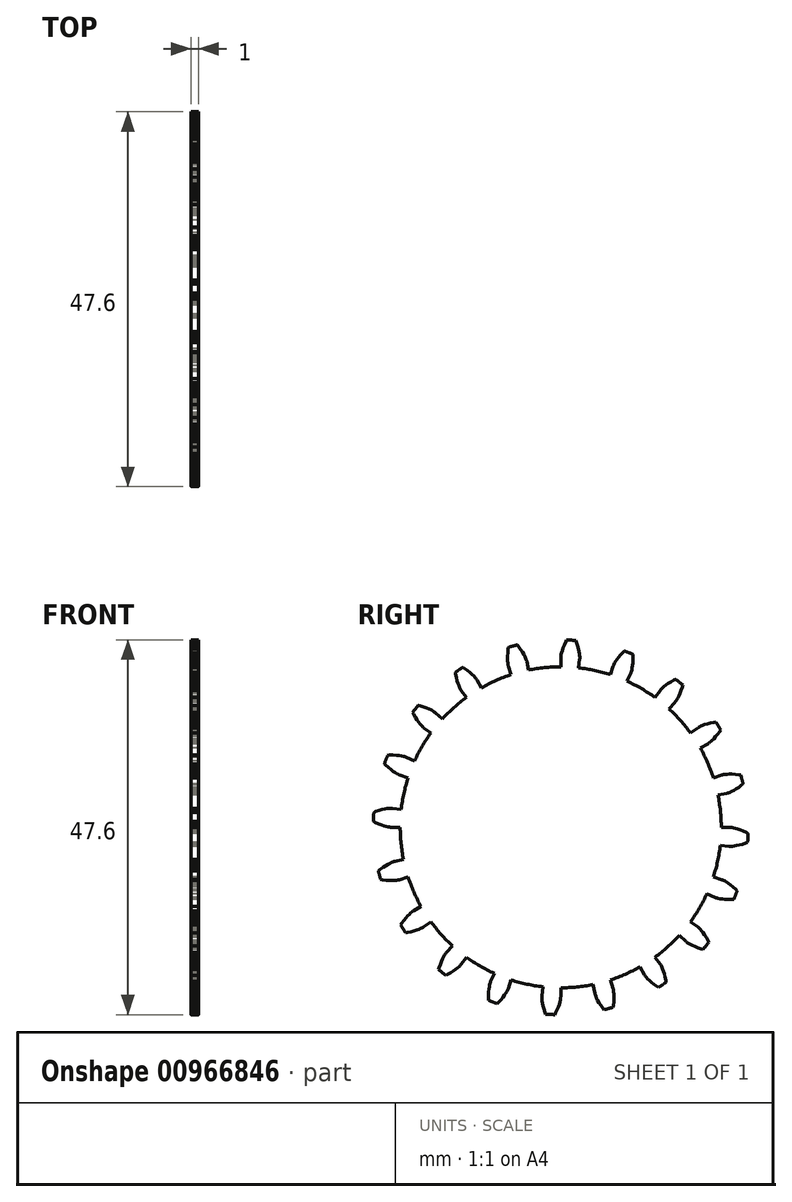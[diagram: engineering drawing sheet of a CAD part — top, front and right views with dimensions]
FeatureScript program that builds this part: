
annotation { "Feature Type Name" : "Feature", "Feature Type Description" : "" }
export const myFeature = defineFeature(function(context is Context, id is Id, definition is map)
    precondition{}
    {
        {
            assignVariable(context, id + "F0", {"name" : "GearThickness", "anyValue" : 1});
        }
        {
            var Q0;
            Q0=qCreatedBy(makeId("Right.planeOp"),FACE);
            var sketch = newSketch(context, id + "F1", { "sketchPlane" : qUnion([Q0])});
            skCircle(sketch, "E0", {"center": v(0, 0) * mm, "radius": 20.39 * mm});
            skCircle(sketch, "E1", {"center": v(0, 0) * mm, "radius": 21.52 * mm, "construction": true});
            skCircle(sketch, "E2", {"center": v(0, 0) * mm, "radius": 22.23 * mm, "construction": true});
            skCircle(sketch, "E3", {"center": v(0, 0) * mm, "radius": 23.81 * mm});
            skLineSegment(sketch, "E4", {"start": v(0, 0) * mm, "end": v(-21.52, 0) * mm, "construction": true});
            skLineSegment(sketch, "E5.1.0", {"start": v(0, 0) * mm, "end": v(-21.5, 1.08) * mm, "construction": true});
            skLineSegment(sketch, "E5.2.0", {"start": v(0, 0) * mm, "end": v(-21.4, 2.15) * mm, "construction": true});
            skLineSegment(sketch, "E5.3.0", {"start": v(0, 0) * mm, "end": v(-21.28, 3.22) * mm, "construction": true});
            skLineSegment(sketch, "E5.4.0", {"start": v(0, 0) * mm, "end": v(-21.09, 4.27) * mm, "construction": true});
            skLineSegment(sketch, "E5.5.0", {"start": v(0, 0) * mm, "end": v(-20.85, 5.32) * mm, "construction": true});
            skLineSegment(sketch, "E5.6.0", {"start": v(0, 0) * mm, "end": v(-20.56, 6.36) * mm, "construction": true});
            skLineSegment(sketch, "E5.7.0", {"start": v(0, 0) * mm, "end": v(-20.21, 7.38) * mm, "construction": true});
            skLineSegment(sketch, "E5.8.0", {"start": v(0, 0) * mm, "end": v(-19.82, 8.38) * mm, "construction": true});
            skLineSegment(sketch, "E5.9.0", {"start": v(0, 0) * mm, "end": v(-19.37, 9.36) * mm, "construction": true});
            skLineSegment(sketch, "E5.10.0", {"start": v(0, 0) * mm, "end": v(-18.88, 10.32) * mm, "construction": true});
            skLineSegment(sketch, "E5.11.0", {"start": v(0, 0) * mm, "end": v(-18.34, 11.25) * mm, "construction": true});
            skLineSegment(sketch, "E5.12.0", {"start": v(0, 0) * mm, "end": v(-17.76, 12.15) * mm, "construction": true});
            skLineSegment(sketch, "E5.13.0", {"start": v(0, 0) * mm, "end": v(-17.13, 13.02) * mm, "construction": true});
            skLineSegment(sketch, "E5.14.0", {"start": v(0, 0) * mm, "end": v(-16.46, 13.86) * mm, "construction": true});
            skLineSegment(sketch, "E5.anchor2", {"start": v(0, 0) * mm, "end": v(-16.46, 13.86) * mm, "construction": true});
            skLineSegment(sketch, "E6", {"start": v(-21.5, 1.08) * mm, "end": v(-21.54, 0) * mm, "construction": true});
            skLineSegment(sketch, "E7", {"start": v(-21.4, 2.15) * mm, "end": v(-21.62, 0) * mm, "construction": true});
            skLineSegment(sketch, "E8", {"start": v(-21.28, 3.22) * mm, "end": v(-21.76, 0.02) * mm, "construction": true});
            skLineSegment(sketch, "E9", {"start": v(-20.85, 5.32) * mm, "end": v(-22.18, 0.11) * mm, "construction": true});
            skLineSegment(sketch, "E10", {"start": v(-20.56, 6.36) * mm, "end": v(-22.46, 0.2) * mm, "construction": true});
            skLineSegment(sketch, "E11", {"start": v(-20.21, 7.38) * mm, "end": v(-22.8, 0.3) * mm, "construction": true});
            skLineSegment(sketch, "E12", {"start": v(-19.82, 8.38) * mm, "end": v(-23.17, 0.45) * mm, "construction": true});
            skLineSegment(sketch, "E13", {"start": v(-19.37, 9.36) * mm, "end": v(-23.59, 0.64) * mm, "construction": true});
            skLineSegment(sketch, "E14", {"start": v(-18.88, 10.32) * mm, "end": v(-24.04, 0.87) * mm, "construction": true});
            skLineSegment(sketch, "E15", {"start": v(-18.34, 11.25) * mm, "end": v(-24.53, 1.16) * mm, "construction": true});
            skLineSegment(sketch, "E16", {"start": v(-21.09, 4.27) * mm, "end": v(-21.94, 0.06) * mm, "construction": true});
            skLineSegment(sketch, "E17", {"start": v(-17.76, 12.15) * mm, "end": v(-25.05, 1.5) * mm, "construction": true});
            skLineSegment(sketch, "E18", {"start": v(-17.13, 13.02) * mm, "end": v(-25.6, 1.89) * mm, "construction": true});
            skLineSegment(sketch, "E19", {"start": v(-16.46, 13.86) * mm, "end": v(-26.16, 2.34) * mm, "construction": true});
            skLineSegment(sketch, "E20", {"start": v(0, 0) * mm, "end": v(-21.48, 1.2) * mm, "construction": true});
            skLineSegment(sketch, "E21", {"start": v(-20.39, 0) * mm, "end": v(-21.52, 0) * mm});
            skLineSegment(sketch, "E22.MirrorCS", {"start": v(-20.26, 2.28) * mm, "end": v(-21.38, 2.4) * mm});
            skLineSegment(sketch, "E23", {"start": v(-21.52, 0) * mm, "end": v(-21.54, 0) * mm});
            skLineSegment(sketch, "E24", {"start": v(-21.54, 0) * mm, "end": v(-21.62, 0) * mm});
            skLineSegment(sketch, "E25", {"start": v(-21.62, 0) * mm, "end": v(-21.76, 0.02) * mm});
            skLineSegment(sketch, "E26", {"start": v(-21.76, 0.02) * mm, "end": v(-21.94, 0.06) * mm});
            skLineSegment(sketch, "E27", {"start": v(-21.94, 0.06) * mm, "end": v(-22.18, 0.11) * mm});
            skLineSegment(sketch, "E28", {"start": v(-22.18, 0.11) * mm, "end": v(-22.46, 0.2) * mm});
            skLineSegment(sketch, "E29", {"start": v(-22.46, 0.2) * mm, "end": v(-22.8, 0.3) * mm});
            skLineSegment(sketch, "E30", {"start": v(-22.8, 0.3) * mm, "end": v(-23.17, 0.45) * mm});
            skLineSegment(sketch, "E31", {"start": v(-23.17, 0.45) * mm, "end": v(-23.59, 0.64) * mm});
            skLineSegment(sketch, "E32", {"start": v(-23.59, 0.64) * mm, "end": v(-24.04, 0.87) * mm});
            skLineSegment(sketch, "E33", {"start": v(-24.04, 0.87) * mm, "end": v(-24.53, 1.16) * mm});
            skLineSegment(sketch, "E34", {"start": v(-24.53, 1.16) * mm, "end": v(-25.05, 1.5) * mm});
            skLineSegment(sketch, "E35", {"start": v(-25.05, 1.5) * mm, "end": v(-25.6, 1.89) * mm});
            skLineSegment(sketch, "E36", {"start": v(-25.6, 1.89) * mm, "end": v(-26.16, 2.34) * mm});
            skLineSegment(sketch, "E37.MirrorCS", {"start": v(-21.38, 2.4) * mm, "end": v(-21.4, 2.41) * mm});
            skLineSegment(sketch, "E38.MirrorCS", {"start": v(-21.4, 2.41) * mm, "end": v(-21.49, 2.41) * mm});
            skLineSegment(sketch, "E39.MirrorCS", {"start": v(-21.49, 2.41) * mm, "end": v(-21.62, 2.41) * mm});
            skLineSegment(sketch, "E40.MirrorCS", {"start": v(-21.62, 2.41) * mm, "end": v(-21.81, 2.4) * mm});
            skLineSegment(sketch, "E41.MirrorCS", {"start": v(-22.05, 2.37) * mm, "end": v(-22.34, 2.32) * mm});
            skLineSegment(sketch, "E42.MirrorCS", {"start": v(-22.34, 2.32) * mm, "end": v(-22.69, 2.25) * mm});
            skLineSegment(sketch, "E43.MirrorCS", {"start": v(-22.69, 2.25) * mm, "end": v(-23.08, 2.15) * mm});
            skLineSegment(sketch, "E44.MirrorCS", {"start": v(-23.08, 2.15) * mm, "end": v(-23.51, 2) * mm});
            skLineSegment(sketch, "E45.MirrorCS", {"start": v(-23.99, 1.82) * mm, "end": v(-24.5, 1.6) * mm});
            skLineSegment(sketch, "E46.MirrorCS", {"start": v(-23.51, 2) * mm, "end": v(-23.99, 1.82) * mm});
            skLineSegment(sketch, "E47.MirrorCS", {"start": v(-24.5, 1.6) * mm, "end": v(-25.06, 1.32) * mm});
            skLineSegment(sketch, "E48.MirrorCS", {"start": v(-25.06, 1.32) * mm, "end": v(-25.64, 0.99) * mm});
            skLineSegment(sketch, "E49.MirrorCS", {"start": v(-25.64, 0.99) * mm, "end": v(-26.26, 0.6) * mm});
            skLineSegment(sketch, "E50.MirrorCS", {"start": v(-21.81, 2.4) * mm, "end": v(-22.05, 2.37) * mm});
            skLineSegment(sketch, "E51.1.0", {"start": v(-19.4, -6.3) * mm, "end": v(-20.46, -6.65) * mm});
            skLineSegment(sketch, "E51.1.1", {"start": v(-23.8, -6.05) * mm, "end": v(-24.24, -6.49) * mm});
            skLineSegment(sketch, "E51.1.2", {"start": v(-19.97, -4.09) * mm, "end": v(-21.08, -4.32) * mm});
            skLineSegment(sketch, "E51.1.3", {"start": v(-23.38, -5.68) * mm, "end": v(-23.8, -6.05) * mm});
            skLineSegment(sketch, "E51.1.4", {"start": v(-23.13, -6.6) * mm, "end": v(-23.69, -6.48) * mm});
            skLineSegment(sketch, "E51.1.5", {"start": v(-23.69, -6.48) * mm, "end": v(-24.28, -6.32) * mm});
            skLineSegment(sketch, "E51.1.6", {"start": v(-22.98, -5.36) * mm, "end": v(-23.38, -5.68) * mm});
            skLineSegment(sketch, "E51.1.7", {"start": v(-24.7, -6.98) * mm, "end": v(-25.16, -7.54) * mm});
            skLineSegment(sketch, "E51.1.8", {"start": v(-22.6, -5.1) * mm, "end": v(-22.98, -5.36) * mm});
            skLineSegment(sketch, "E51.1.9", {"start": v(-24.92, -6.11) * mm, "end": v(-25.6, -5.86) * mm});
            skLineSegment(sketch, "E51.1.10", {"start": v(-24.24, -6.49) * mm, "end": v(-24.7, -6.98) * mm});
            skLineSegment(sketch, "E51.1.11", {"start": v(-22.63, -6.68) * mm, "end": v(-23.13, -6.6) * mm});
            skLineSegment(sketch, "E51.1.12", {"start": v(-24.28, -6.32) * mm, "end": v(-24.92, -6.11) * mm});
            skLineSegment(sketch, "E51.1.13", {"start": v(-21.7, -4.56) * mm, "end": v(-21.97, -4.7) * mm});
            skLineSegment(sketch, "E51.1.14", {"start": v(-21.97, -4.7) * mm, "end": v(-22.27, -4.87) * mm});
            skLineSegment(sketch, "E51.1.15", {"start": v(-22.27, -4.87) * mm, "end": v(-22.6, -5.1) * mm});
            skLineSegment(sketch, "E51.1.16", {"start": v(-21.77, -6.76) * mm, "end": v(-22.18, -6.73) * mm});
            skLineSegment(sketch, "E51.1.17", {"start": v(-21.42, -6.76) * mm, "end": v(-21.77, -6.76) * mm});
            skLineSegment(sketch, "E51.1.18", {"start": v(-22.18, -6.73) * mm, "end": v(-22.63, -6.68) * mm});
            skLineSegment(sketch, "E51.1.19", {"start": v(-21.49, -4.46) * mm, "end": v(-21.7, -4.56) * mm});
            skLineSegment(sketch, "E51.1.20", {"start": v(-21.31, -4.39) * mm, "end": v(-21.49, -4.46) * mm});
            skLineSegment(sketch, "E51.1.21", {"start": v(-21.13, -6.75) * mm, "end": v(-21.42, -6.76) * mm});
            skLineSegment(sketch, "E51.1.22", {"start": v(-20.89, -6.73) * mm, "end": v(-21.13, -6.75) * mm});
            skLineSegment(sketch, "E51.1.23", {"start": v(-20.57, -6.68) * mm, "end": v(-20.7, -6.7) * mm});
            skLineSegment(sketch, "E51.1.24", {"start": v(-21.08, -4.32) * mm, "end": v(-21.1, -4.32) * mm});
            skLineSegment(sketch, "E51.1.25", {"start": v(-21.1, -4.32) * mm, "end": v(-21.18, -4.34) * mm});
            skLineSegment(sketch, "E51.1.26", {"start": v(-20.7, -6.7) * mm, "end": v(-20.89, -6.73) * mm});
            skLineSegment(sketch, "E51.1.27", {"start": v(-21.18, -4.34) * mm, "end": v(-21.31, -4.39) * mm});
            skLineSegment(sketch, "E51.1.28", {"start": v(-20.49, -6.66) * mm, "end": v(-20.57, -6.68) * mm});
            skLineSegment(sketch, "E51.1.29", {"start": v(-20.46, -6.65) * mm, "end": v(-20.49, -6.66) * mm});
            skLineSegment(sketch, "E51.2.0", {"start": v(-16.5, -11.98) * mm, "end": v(-17.4, -12.65) * mm});
            skLineSegment(sketch, "E51.2.1", {"start": v(-20.76, -13.11) * mm, "end": v(-21.05, -13.66) * mm});
            skLineSegment(sketch, "E51.2.2", {"start": v(-17.73, -10.06) * mm, "end": v(-18.71, -10.62) * mm});
            skLineSegment(sketch, "E51.2.3", {"start": v(-20.48, -12.62) * mm, "end": v(-20.76, -13.11) * mm});
            skLineSegment(sketch, "E51.2.4", {"start": v(-19.96, -13.42) * mm, "end": v(-20.53, -13.48) * mm});
            skLineSegment(sketch, "E51.2.5", {"start": v(-20.53, -13.48) * mm, "end": v(-21.14, -13.51) * mm});
            skLineSegment(sketch, "E51.2.6", {"start": v(-20.2, -12.2) * mm, "end": v(-20.48, -12.62) * mm});
            skLineSegment(sketch, "E51.2.7", {"start": v(-21.33, -14.27) * mm, "end": v(-21.6, -14.95) * mm});
            skLineSegment(sketch, "E51.2.8", {"start": v(-19.93, -11.83) * mm, "end": v(-20.2, -12.2) * mm});
            skLineSegment(sketch, "E51.2.9", {"start": v(-21.82, -13.52) * mm, "end": v(-22.54, -13.48) * mm});
            skLineSegment(sketch, "E51.2.10", {"start": v(-21.05, -13.66) * mm, "end": v(-21.33, -14.27) * mm});
            skLineSegment(sketch, "E51.2.11", {"start": v(-19.46, -13.35) * mm, "end": v(-19.96, -13.42) * mm});
            skLineSegment(sketch, "E51.2.12", {"start": v(-21.14, -13.51) * mm, "end": v(-21.82, -13.52) * mm});
            skLineSegment(sketch, "E51.2.13", {"start": v(-19.24, -11.04) * mm, "end": v(-19.44, -11.25) * mm});
            skLineSegment(sketch, "E51.2.14", {"start": v(-19.44, -11.25) * mm, "end": v(-19.68, -11.51) * mm});
            skLineSegment(sketch, "E51.2.15", {"start": v(-19.68, -11.51) * mm, "end": v(-19.93, -11.83) * mm});
            skLineSegment(sketch, "E51.2.16", {"start": v(-18.62, -13.15) * mm, "end": v(-19.01, -13.25) * mm});
            skLineSegment(sketch, "E51.2.17", {"start": v(-18.29, -13.05) * mm, "end": v(-18.62, -13.15) * mm});
            skLineSegment(sketch, "E51.2.18", {"start": v(-19.01, -13.25) * mm, "end": v(-19.46, -13.35) * mm});
            skLineSegment(sketch, "E51.2.19", {"start": v(-19.06, -10.88) * mm, "end": v(-19.24, -11.04) * mm});
            skLineSegment(sketch, "E51.2.20", {"start": v(-18.91, -10.76) * mm, "end": v(-19.06, -10.88) * mm});
            skLineSegment(sketch, "E51.2.21", {"start": v(-18, -12.95) * mm, "end": v(-18.29, -13.05) * mm});
            skLineSegment(sketch, "E51.2.22", {"start": v(-17.79, -12.85) * mm, "end": v(-18, -12.95) * mm});
            skLineSegment(sketch, "E51.2.23", {"start": v(-17.5, -12.7) * mm, "end": v(-17.62, -12.77) * mm});
            skLineSegment(sketch, "E51.2.24", {"start": v(-18.71, -10.62) * mm, "end": v(-18.74, -10.63) * mm});
            skLineSegment(sketch, "E51.2.25", {"start": v(-18.74, -10.63) * mm, "end": v(-18.8, -10.68) * mm});
            skLineSegment(sketch, "E51.2.26", {"start": v(-17.62, -12.77) * mm, "end": v(-17.79, -12.85) * mm});
            skLineSegment(sketch, "E51.2.27", {"start": v(-18.8, -10.68) * mm, "end": v(-18.91, -10.76) * mm});
            skLineSegment(sketch, "E51.2.28", {"start": v(-17.43, -12.66) * mm, "end": v(-17.5, -12.7) * mm});
            skLineSegment(sketch, "E51.2.29", {"start": v(-17.4, -12.65) * mm, "end": v(-17.43, -12.66) * mm});
            skLineSegment(sketch, "E51.3.0", {"start": v(-11.98, -16.5) * mm, "end": v(-12.65, -17.4) * mm});
            skLineSegment(sketch, "E51.3.1", {"start": v(-15.7, -18.89) * mm, "end": v(-15.8, -19.5) * mm});
            skLineSegment(sketch, "E51.3.2", {"start": v(-13.76, -15.05) * mm, "end": v(-14.52, -15.88) * mm});
            skLineSegment(sketch, "E51.3.3", {"start": v(-15.57, -18.33) * mm, "end": v(-15.7, -18.89) * mm});
            skLineSegment(sketch, "E51.3.4", {"start": v(-14.84, -18.94) * mm, "end": v(-15.35, -19.16) * mm});
            skLineSegment(sketch, "E51.3.5", {"start": v(-15.35, -19.16) * mm, "end": v(-15.93, -19.39) * mm});
            skLineSegment(sketch, "E51.3.6", {"start": v(-15.44, -17.84) * mm, "end": v(-15.57, -18.33) * mm});
            skLineSegment(sketch, "E51.3.7", {"start": v(-15.87, -20.16) * mm, "end": v(-15.92, -20.89) * mm});
            skLineSegment(sketch, "E51.3.8", {"start": v(-15.3, -17.4) * mm, "end": v(-15.44, -17.84) * mm});
            skLineSegment(sketch, "E51.3.9", {"start": v(-16.57, -19.6) * mm, "end": v(-17.27, -19.79) * mm});
            skLineSegment(sketch, "E51.3.10", {"start": v(-15.8, -19.5) * mm, "end": v(-15.87, -20.16) * mm});
            skLineSegment(sketch, "E51.3.11", {"start": v(-14.38, -18.7) * mm, "end": v(-14.84, -18.94) * mm});
            skLineSegment(sketch, "E51.3.12", {"start": v(-15.93, -19.39) * mm, "end": v(-16.57, -19.6) * mm});
            skLineSegment(sketch, "E51.3.13", {"start": v(-14.88, -16.45) * mm, "end": v(-15.01, -16.71) * mm});
            skLineSegment(sketch, "E51.3.14", {"start": v(-15.01, -16.71) * mm, "end": v(-15.15, -17.03) * mm});
            skLineSegment(sketch, "E51.3.15", {"start": v(-15.15, -17.03) * mm, "end": v(-15.3, -17.4) * mm});
            skLineSegment(sketch, "E51.3.16", {"start": v(-13.64, -18.26) * mm, "end": v(-13.98, -18.48) * mm});
            skLineSegment(sketch, "E51.3.17", {"start": v(-13.36, -18.06) * mm, "end": v(-13.64, -18.26) * mm});
            skLineSegment(sketch, "E51.3.18", {"start": v(-13.98, -18.48) * mm, "end": v(-14.38, -18.7) * mm});
            skLineSegment(sketch, "E51.3.19", {"start": v(-14.76, -16.24) * mm, "end": v(-14.88, -16.45) * mm});
            skLineSegment(sketch, "E51.3.20", {"start": v(-14.66, -16.08) * mm, "end": v(-14.76, -16.24) * mm});
            skLineSegment(sketch, "E51.3.21", {"start": v(-13.13, -17.88) * mm, "end": v(-13.36, -18.06) * mm});
            skLineSegment(sketch, "E51.3.22", {"start": v(-12.94, -17.72) * mm, "end": v(-13.13, -17.88) * mm});
            skLineSegment(sketch, "E51.3.23", {"start": v(-12.72, -17.5) * mm, "end": v(-12.8, -17.59) * mm});
            skLineSegment(sketch, "E51.3.24", {"start": v(-14.52, -15.88) * mm, "end": v(-14.53, -15.9) * mm});
            skLineSegment(sketch, "E51.3.25", {"start": v(-14.53, -15.9) * mm, "end": v(-14.58, -15.97) * mm});
            skLineSegment(sketch, "E51.3.26", {"start": v(-12.8, -17.59) * mm, "end": v(-12.94, -17.72) * mm});
            skLineSegment(sketch, "E51.3.27", {"start": v(-14.58, -15.97) * mm, "end": v(-14.66, -16.08) * mm});
            skLineSegment(sketch, "E51.3.28", {"start": v(-12.66, -17.43) * mm, "end": v(-12.72, -17.5) * mm});
            skLineSegment(sketch, "E51.3.29", {"start": v(-12.65, -17.4) * mm, "end": v(-12.66, -17.43) * mm});
            skLineSegment(sketch, "E51.4.0", {"start": v(-6.3, -19.4) * mm, "end": v(-6.65, -20.46) * mm});
            skLineSegment(sketch, "E51.4.1", {"start": v(-9.1, -22.81) * mm, "end": v(-9, -23.42) * mm});
            skLineSegment(sketch, "E51.4.2", {"start": v(-8.43, -18.56) * mm, "end": v(-8.9, -19.6) * mm});
            skLineSegment(sketch, "E51.4.3", {"start": v(-9.15, -22.25) * mm, "end": v(-9.1, -22.81) * mm});
            skLineSegment(sketch, "E51.4.4", {"start": v(-8.26, -22.6) * mm, "end": v(-8.68, -22.97) * mm});
            skLineSegment(sketch, "E51.4.5", {"start": v(-8.68, -22.97) * mm, "end": v(-9.16, -23.36) * mm});
            skLineSegment(sketch, "E51.4.6", {"start": v(-9.17, -21.74) * mm, "end": v(-9.15, -22.25) * mm});
            skLineSegment(sketch, "E51.4.7", {"start": v(-8.87, -24.08) * mm, "end": v(-8.69, -24.79) * mm});
            skLineSegment(sketch, "E51.4.8", {"start": v(-9.17, -21.28) * mm, "end": v(-9.17, -21.74) * mm});
            skLineSegment(sketch, "E51.4.9", {"start": v(-9.7, -23.76) * mm, "end": v(-10.31, -24.16) * mm});
            skLineSegment(sketch, "E51.4.10", {"start": v(-9, -23.42) * mm, "end": v(-8.87, -24.08) * mm});
            skLineSegment(sketch, "E51.4.11", {"start": v(-7.9, -22.23) * mm, "end": v(-8.26, -22.6) * mm});
            skLineSegment(sketch, "E51.4.12", {"start": v(-9.16, -23.36) * mm, "end": v(-9.7, -23.76) * mm});
            skLineSegment(sketch, "E51.4.13", {"start": v(-9.07, -20.24) * mm, "end": v(-9.12, -20.53) * mm});
            skLineSegment(sketch, "E51.4.14", {"start": v(-9.12, -20.53) * mm, "end": v(-9.15, -20.88) * mm});
            skLineSegment(sketch, "E51.4.15", {"start": v(-9.15, -20.88) * mm, "end": v(-9.17, -21.28) * mm});
            skLineSegment(sketch, "E51.4.16", {"start": v(-7.33, -21.59) * mm, "end": v(-7.59, -21.9) * mm});
            skLineSegment(sketch, "E51.4.17", {"start": v(-7.12, -21.3) * mm, "end": v(-7.33, -21.59) * mm});
            skLineSegment(sketch, "E51.4.18", {"start": v(-7.59, -21.9) * mm, "end": v(-7.9, -22.23) * mm});
            skLineSegment(sketch, "E51.4.19", {"start": v(-9.02, -20) * mm, "end": v(-9.07, -20.24) * mm});
            skLineSegment(sketch, "E51.4.20", {"start": v(-8.98, -19.82) * mm, "end": v(-9.02, -20) * mm});
            skLineSegment(sketch, "E51.4.21", {"start": v(-6.96, -21.06) * mm, "end": v(-7.12, -21.3) * mm});
            skLineSegment(sketch, "E51.4.22", {"start": v(-6.84, -20.85) * mm, "end": v(-6.96, -21.06) * mm});
            skLineSegment(sketch, "E51.4.23", {"start": v(-6.69, -20.56) * mm, "end": v(-6.75, -20.69) * mm});
            skLineSegment(sketch, "E51.4.24", {"start": v(-8.9, -19.6) * mm, "end": v(-8.9, -19.62) * mm});
            skLineSegment(sketch, "E51.4.25", {"start": v(-8.9, -19.62) * mm, "end": v(-8.94, -19.7) * mm});
            skLineSegment(sketch, "E51.4.26", {"start": v(-6.75, -20.69) * mm, "end": v(-6.84, -20.85) * mm});
            skLineSegment(sketch, "E51.4.27", {"start": v(-8.94, -19.7) * mm, "end": v(-8.98, -19.82) * mm});
            skLineSegment(sketch, "E51.4.28", {"start": v(-6.66, -20.49) * mm, "end": v(-6.69, -20.56) * mm});
            skLineSegment(sketch, "E51.4.29", {"start": v(-6.65, -20.46) * mm, "end": v(-6.66, -20.49) * mm});
            skLineSegment(sketch, "E51.5.0", {"start": v(0, -20.39) * mm, "end": v(0, -21.52) * mm});
            skLineSegment(sketch, "E51.5.1", {"start": v(-1.6, -24.5) * mm, "end": v(-1.32, -25.06) * mm});
            skLineSegment(sketch, "E51.5.2", {"start": v(-2.28, -20.26) * mm, "end": v(-2.4, -21.38) * mm});
            skLineSegment(sketch, "E51.5.3", {"start": v(-1.82, -23.99) * mm, "end": v(-1.6, -24.5) * mm});
            skLineSegment(sketch, "E51.5.4", {"start": v(-0.87, -24.04) * mm, "end": v(-1.16, -24.53) * mm});
            skLineSegment(sketch, "E51.5.5", {"start": v(-1.16, -24.53) * mm, "end": v(-1.5, -25.05) * mm});
            skLineSegment(sketch, "E51.5.6", {"start": v(-2, -23.51) * mm, "end": v(-1.82, -23.99) * mm});
            skLineSegment(sketch, "E51.5.7", {"start": v(-0.99, -25.64) * mm, "end": v(-0.6, -26.26) * mm});
            skLineSegment(sketch, "E51.5.8", {"start": v(-2.15, -23.08) * mm, "end": v(-2, -23.51) * mm});
            skLineSegment(sketch, "E51.5.9", {"start": v(-1.89, -25.6) * mm, "end": v(-2.34, -26.16) * mm});
            skLineSegment(sketch, "E51.5.10", {"start": v(-1.32, -25.06) * mm, "end": v(-0.99, -25.64) * mm});
            skLineSegment(sketch, "E51.5.11", {"start": v(-0.64, -23.59) * mm, "end": v(-0.87, -24.04) * mm});
            skLineSegment(sketch, "E51.5.12", {"start": v(-1.5, -25.05) * mm, "end": v(-1.89, -25.6) * mm});
            skLineSegment(sketch, "E51.5.13", {"start": v(-2.37, -22.05) * mm, "end": v(-2.32, -22.34) * mm});
            skLineSegment(sketch, "E51.5.14", {"start": v(-2.32, -22.34) * mm, "end": v(-2.25, -22.69) * mm});
            skLineSegment(sketch, "E51.5.15", {"start": v(-2.25, -22.69) * mm, "end": v(-2.15, -23.08) * mm});
            skLineSegment(sketch, "E51.5.16", {"start": v(-0.3, -22.8) * mm, "end": v(-0.45, -23.17) * mm});
            skLineSegment(sketch, "E51.5.17", {"start": v(-0.2, -22.46) * mm, "end": v(-0.3, -22.8) * mm});
            skLineSegment(sketch, "E51.5.18", {"start": v(-0.45, -23.17) * mm, "end": v(-0.64, -23.59) * mm});
            skLineSegment(sketch, "E51.5.19", {"start": v(-2.4, -21.81) * mm, "end": v(-2.37, -22.05) * mm});
            skLineSegment(sketch, "E51.5.20", {"start": v(-2.41, -21.62) * mm, "end": v(-2.4, -21.81) * mm});
            skLineSegment(sketch, "E51.5.21", {"start": v(-0.11, -22.18) * mm, "end": v(-0.2, -22.46) * mm});
            skLineSegment(sketch, "E51.5.22", {"start": v(-0.06, -21.94) * mm, "end": v(-0.11, -22.18) * mm});
            skLineSegment(sketch, "E51.5.23", {"start": v(0, -21.62) * mm, "end": v(-0.02, -21.76) * mm});
            skLineSegment(sketch, "E51.5.24", {"start": v(-2.4, -21.38) * mm, "end": v(-2.41, -21.4) * mm});
            skLineSegment(sketch, "E51.5.25", {"start": v(-2.41, -21.4) * mm, "end": v(-2.41, -21.49) * mm});
            skLineSegment(sketch, "E51.5.26", {"start": v(-0.02, -21.76) * mm, "end": v(-0.06, -21.94) * mm});
            skLineSegment(sketch, "E51.5.27", {"start": v(-2.41, -21.49) * mm, "end": v(-2.41, -21.62) * mm});
            skLineSegment(sketch, "E51.5.28", {"start": v(0, -21.54) * mm, "end": v(0, -21.62) * mm});
            skLineSegment(sketch, "E51.5.29", {"start": v(0, -21.52) * mm, "end": v(0, -21.54) * mm});
            skLineSegment(sketch, "E51.6.0", {"start": v(6.3, -19.4) * mm, "end": v(6.65, -20.46) * mm});
            skLineSegment(sketch, "E51.6.1", {"start": v(6.05, -23.8) * mm, "end": v(6.49, -24.24) * mm});
            skLineSegment(sketch, "E51.6.2", {"start": v(4.09, -19.97) * mm, "end": v(4.32, -21.08) * mm});
            skLineSegment(sketch, "E51.6.3", {"start": v(5.68, -23.38) * mm, "end": v(6.05, -23.8) * mm});
            skLineSegment(sketch, "E51.6.4", {"start": v(6.6, -23.13) * mm, "end": v(6.48, -23.69) * mm});
            skLineSegment(sketch, "E51.6.5", {"start": v(6.48, -23.69) * mm, "end": v(6.32, -24.28) * mm});
            skLineSegment(sketch, "E51.6.6", {"start": v(5.36, -22.98) * mm, "end": v(5.68, -23.38) * mm});
            skLineSegment(sketch, "E51.6.7", {"start": v(6.98, -24.7) * mm, "end": v(7.54, -25.16) * mm});
            skLineSegment(sketch, "E51.6.8", {"start": v(5.1, -22.6) * mm, "end": v(5.36, -22.98) * mm});
            skLineSegment(sketch, "E51.6.9", {"start": v(6.11, -24.92) * mm, "end": v(5.86, -25.6) * mm});
            skLineSegment(sketch, "E51.6.10", {"start": v(6.49, -24.24) * mm, "end": v(6.98, -24.7) * mm});
            skLineSegment(sketch, "E51.6.11", {"start": v(6.68, -22.63) * mm, "end": v(6.6, -23.13) * mm});
            skLineSegment(sketch, "E51.6.12", {"start": v(6.32, -24.28) * mm, "end": v(6.11, -24.92) * mm});
            skLineSegment(sketch, "E51.6.13", {"start": v(4.56, -21.7) * mm, "end": v(4.7, -21.97) * mm});
            skLineSegment(sketch, "E51.6.14", {"start": v(4.7, -21.97) * mm, "end": v(4.87, -22.27) * mm});
            skLineSegment(sketch, "E51.6.15", {"start": v(4.87, -22.27) * mm, "end": v(5.1, -22.6) * mm});
            skLineSegment(sketch, "E51.6.16", {"start": v(6.76, -21.77) * mm, "end": v(6.73, -22.18) * mm});
            skLineSegment(sketch, "E51.6.17", {"start": v(6.76, -21.42) * mm, "end": v(6.76, -21.77) * mm});
            skLineSegment(sketch, "E51.6.18", {"start": v(6.73, -22.18) * mm, "end": v(6.68, -22.63) * mm});
            skLineSegment(sketch, "E51.6.19", {"start": v(4.46, -21.49) * mm, "end": v(4.56, -21.7) * mm});
            skLineSegment(sketch, "E51.6.20", {"start": v(4.39, -21.31) * mm, "end": v(4.46, -21.49) * mm});
            skLineSegment(sketch, "E51.6.21", {"start": v(6.75, -21.13) * mm, "end": v(6.76, -21.42) * mm});
            skLineSegment(sketch, "E51.6.22", {"start": v(6.73, -20.89) * mm, "end": v(6.75, -21.13) * mm});
            skLineSegment(sketch, "E51.6.23", {"start": v(6.68, -20.57) * mm, "end": v(6.7, -20.7) * mm});
            skLineSegment(sketch, "E51.6.24", {"start": v(4.32, -21.08) * mm, "end": v(4.32, -21.1) * mm});
            skLineSegment(sketch, "E51.6.25", {"start": v(4.32, -21.1) * mm, "end": v(4.34, -21.18) * mm});
            skLineSegment(sketch, "E51.6.26", {"start": v(6.7, -20.7) * mm, "end": v(6.73, -20.89) * mm});
            skLineSegment(sketch, "E51.6.27", {"start": v(4.34, -21.18) * mm, "end": v(4.39, -21.31) * mm});
            skLineSegment(sketch, "E51.6.28", {"start": v(6.66, -20.49) * mm, "end": v(6.68, -20.57) * mm});
            skLineSegment(sketch, "E51.6.29", {"start": v(6.65, -20.46) * mm, "end": v(6.66, -20.49) * mm});
            skLineSegment(sketch, "E51.7.0", {"start": v(11.98, -16.5) * mm, "end": v(12.65, -17.4) * mm});
            skLineSegment(sketch, "E51.7.1", {"start": v(13.11, -20.76) * mm, "end": v(13.66, -21.05) * mm});
            skLineSegment(sketch, "E51.7.2", {"start": v(10.06, -17.73) * mm, "end": v(10.62, -18.71) * mm});
            skLineSegment(sketch, "E51.7.3", {"start": v(12.62, -20.48) * mm, "end": v(13.11, -20.76) * mm});
            skLineSegment(sketch, "E51.7.4", {"start": v(13.42, -19.96) * mm, "end": v(13.48, -20.53) * mm});
            skLineSegment(sketch, "E51.7.5", {"start": v(13.48, -20.53) * mm, "end": v(13.51, -21.14) * mm});
            skLineSegment(sketch, "E51.7.6", {"start": v(12.2, -20.2) * mm, "end": v(12.62, -20.48) * mm});
            skLineSegment(sketch, "E51.7.7", {"start": v(14.27, -21.33) * mm, "end": v(14.95, -21.6) * mm});
            skLineSegment(sketch, "E51.7.8", {"start": v(11.83, -19.93) * mm, "end": v(12.2, -20.2) * mm});
            skLineSegment(sketch, "E51.7.9", {"start": v(13.52, -21.82) * mm, "end": v(13.48, -22.54) * mm});
            skLineSegment(sketch, "E51.7.10", {"start": v(13.66, -21.05) * mm, "end": v(14.27, -21.33) * mm});
            skLineSegment(sketch, "E51.7.11", {"start": v(13.35, -19.46) * mm, "end": v(13.42, -19.96) * mm});
            skLineSegment(sketch, "E51.7.12", {"start": v(13.51, -21.14) * mm, "end": v(13.52, -21.82) * mm});
            skLineSegment(sketch, "E51.7.13", {"start": v(11.04, -19.24) * mm, "end": v(11.25, -19.44) * mm});
            skLineSegment(sketch, "E51.7.14", {"start": v(11.25, -19.44) * mm, "end": v(11.51, -19.68) * mm});
            skLineSegment(sketch, "E51.7.15", {"start": v(11.51, -19.68) * mm, "end": v(11.83, -19.93) * mm});
            skLineSegment(sketch, "E51.7.16", {"start": v(13.15, -18.62) * mm, "end": v(13.25, -19.01) * mm});
            skLineSegment(sketch, "E51.7.17", {"start": v(13.05, -18.29) * mm, "end": v(13.15, -18.62) * mm});
            skLineSegment(sketch, "E51.7.18", {"start": v(13.25, -19.01) * mm, "end": v(13.35, -19.46) * mm});
            skLineSegment(sketch, "E51.7.19", {"start": v(10.88, -19.06) * mm, "end": v(11.04, -19.24) * mm});
            skLineSegment(sketch, "E51.7.20", {"start": v(10.76, -18.91) * mm, "end": v(10.88, -19.06) * mm});
            skLineSegment(sketch, "E51.7.21", {"start": v(12.95, -18) * mm, "end": v(13.05, -18.29) * mm});
            skLineSegment(sketch, "E51.7.22", {"start": v(12.85, -17.79) * mm, "end": v(12.95, -18) * mm});
            skLineSegment(sketch, "E51.7.23", {"start": v(12.7, -17.5) * mm, "end": v(12.77, -17.62) * mm});
            skLineSegment(sketch, "E51.7.24", {"start": v(10.62, -18.71) * mm, "end": v(10.63, -18.74) * mm});
            skLineSegment(sketch, "E51.7.25", {"start": v(10.63, -18.74) * mm, "end": v(10.68, -18.8) * mm});
            skLineSegment(sketch, "E51.7.26", {"start": v(12.77, -17.62) * mm, "end": v(12.85, -17.79) * mm});
            skLineSegment(sketch, "E51.7.27", {"start": v(10.68, -18.8) * mm, "end": v(10.76, -18.91) * mm});
            skLineSegment(sketch, "E51.7.28", {"start": v(12.66, -17.43) * mm, "end": v(12.7, -17.5) * mm});
            skLineSegment(sketch, "E51.7.29", {"start": v(12.65, -17.4) * mm, "end": v(12.66, -17.43) * mm});
            skLineSegment(sketch, "E51.8.0", {"start": v(16.5, -11.98) * mm, "end": v(17.4, -12.65) * mm});
            skLineSegment(sketch, "E51.8.1", {"start": v(18.89, -15.7) * mm, "end": v(19.5, -15.8) * mm});
            skLineSegment(sketch, "E51.8.2", {"start": v(15.05, -13.76) * mm, "end": v(15.88, -14.52) * mm});
            skLineSegment(sketch, "E51.8.3", {"start": v(18.33, -15.57) * mm, "end": v(18.89, -15.7) * mm});
            skLineSegment(sketch, "E51.8.4", {"start": v(18.94, -14.84) * mm, "end": v(19.16, -15.35) * mm});
            skLineSegment(sketch, "E51.8.5", {"start": v(19.16, -15.35) * mm, "end": v(19.39, -15.93) * mm});
            skLineSegment(sketch, "E51.8.6", {"start": v(17.84, -15.44) * mm, "end": v(18.33, -15.57) * mm});
            skLineSegment(sketch, "E51.8.7", {"start": v(20.16, -15.87) * mm, "end": v(20.89, -15.92) * mm});
            skLineSegment(sketch, "E51.8.8", {"start": v(17.4, -15.3) * mm, "end": v(17.84, -15.44) * mm});
            skLineSegment(sketch, "E51.8.9", {"start": v(19.6, -16.57) * mm, "end": v(19.79, -17.27) * mm});
            skLineSegment(sketch, "E51.8.10", {"start": v(19.5, -15.8) * mm, "end": v(20.16, -15.87) * mm});
            skLineSegment(sketch, "E51.8.11", {"start": v(18.7, -14.38) * mm, "end": v(18.94, -14.84) * mm});
            skLineSegment(sketch, "E51.8.12", {"start": v(19.39, -15.93) * mm, "end": v(19.6, -16.57) * mm});
            skLineSegment(sketch, "E51.8.13", {"start": v(16.45, -14.88) * mm, "end": v(16.71, -15.01) * mm});
            skLineSegment(sketch, "E51.8.14", {"start": v(16.71, -15.01) * mm, "end": v(17.03, -15.15) * mm});
            skLineSegment(sketch, "E51.8.15", {"start": v(17.03, -15.15) * mm, "end": v(17.4, -15.3) * mm});
            skLineSegment(sketch, "E51.8.16", {"start": v(18.26, -13.64) * mm, "end": v(18.48, -13.98) * mm});
            skLineSegment(sketch, "E51.8.17", {"start": v(18.06, -13.36) * mm, "end": v(18.26, -13.64) * mm});
            skLineSegment(sketch, "E51.8.18", {"start": v(18.48, -13.98) * mm, "end": v(18.7, -14.38) * mm});
            skLineSegment(sketch, "E51.8.19", {"start": v(16.24, -14.76) * mm, "end": v(16.45, -14.88) * mm});
            skLineSegment(sketch, "E51.8.20", {"start": v(16.08, -14.66) * mm, "end": v(16.24, -14.76) * mm});
            skLineSegment(sketch, "E51.8.21", {"start": v(17.88, -13.13) * mm, "end": v(18.06, -13.36) * mm});
            skLineSegment(sketch, "E51.8.22", {"start": v(17.72, -12.94) * mm, "end": v(17.88, -13.13) * mm});
            skLineSegment(sketch, "E51.8.23", {"start": v(17.5, -12.72) * mm, "end": v(17.59, -12.8) * mm});
            skLineSegment(sketch, "E51.8.24", {"start": v(15.88, -14.52) * mm, "end": v(15.9, -14.53) * mm});
            skLineSegment(sketch, "E51.8.25", {"start": v(15.9, -14.53) * mm, "end": v(15.97, -14.58) * mm});
            skLineSegment(sketch, "E51.8.26", {"start": v(17.59, -12.8) * mm, "end": v(17.72, -12.94) * mm});
            skLineSegment(sketch, "E51.8.27", {"start": v(15.97, -14.58) * mm, "end": v(16.08, -14.66) * mm});
            skLineSegment(sketch, "E51.8.28", {"start": v(17.43, -12.66) * mm, "end": v(17.5, -12.72) * mm});
            skLineSegment(sketch, "E51.8.29", {"start": v(17.4, -12.65) * mm, "end": v(17.43, -12.66) * mm});
            skLineSegment(sketch, "E51.9.0", {"start": v(19.4, -6.3) * mm, "end": v(20.46, -6.65) * mm});
            skLineSegment(sketch, "E51.9.1", {"start": v(22.81, -9.1) * mm, "end": v(23.42, -9) * mm});
            skLineSegment(sketch, "E51.9.2", {"start": v(18.56, -8.43) * mm, "end": v(19.6, -8.9) * mm});
            skLineSegment(sketch, "E51.9.3", {"start": v(22.25, -9.15) * mm, "end": v(22.81, -9.1) * mm});
            skLineSegment(sketch, "E51.9.4", {"start": v(22.6, -8.26) * mm, "end": v(22.97, -8.68) * mm});
            skLineSegment(sketch, "E51.9.5", {"start": v(22.97, -8.68) * mm, "end": v(23.36, -9.16) * mm});
            skLineSegment(sketch, "E51.9.6", {"start": v(21.74, -9.17) * mm, "end": v(22.25, -9.15) * mm});
            skLineSegment(sketch, "E51.9.7", {"start": v(24.08, -8.87) * mm, "end": v(24.79, -8.69) * mm});
            skLineSegment(sketch, "E51.9.8", {"start": v(21.28, -9.17) * mm, "end": v(21.74, -9.17) * mm});
            skLineSegment(sketch, "E51.9.9", {"start": v(23.76, -9.7) * mm, "end": v(24.16, -10.31) * mm});
            skLineSegment(sketch, "E51.9.10", {"start": v(23.42, -9) * mm, "end": v(24.08, -8.87) * mm});
            skLineSegment(sketch, "E51.9.11", {"start": v(22.23, -7.9) * mm, "end": v(22.6, -8.26) * mm});
            skLineSegment(sketch, "E51.9.12", {"start": v(23.36, -9.16) * mm, "end": v(23.76, -9.7) * mm});
            skLineSegment(sketch, "E51.9.13", {"start": v(20.24, -9.07) * mm, "end": v(20.53, -9.12) * mm});
            skLineSegment(sketch, "E51.9.14", {"start": v(20.53, -9.12) * mm, "end": v(20.88, -9.15) * mm});
            skLineSegment(sketch, "E51.9.15", {"start": v(20.88, -9.15) * mm, "end": v(21.28, -9.17) * mm});
            skLineSegment(sketch, "E51.9.16", {"start": v(21.59, -7.33) * mm, "end": v(21.9, -7.59) * mm});
            skLineSegment(sketch, "E51.9.17", {"start": v(21.3, -7.12) * mm, "end": v(21.59, -7.33) * mm});
            skLineSegment(sketch, "E51.9.18", {"start": v(21.9, -7.59) * mm, "end": v(22.23, -7.9) * mm});
            skLineSegment(sketch, "E51.9.19", {"start": v(20, -9.02) * mm, "end": v(20.24, -9.07) * mm});
            skLineSegment(sketch, "E51.9.20", {"start": v(19.82, -8.98) * mm, "end": v(20, -9.02) * mm});
            skLineSegment(sketch, "E51.9.21", {"start": v(21.06, -6.96) * mm, "end": v(21.3, -7.12) * mm});
            skLineSegment(sketch, "E51.9.22", {"start": v(20.85, -6.84) * mm, "end": v(21.06, -6.96) * mm});
            skLineSegment(sketch, "E51.9.23", {"start": v(20.56, -6.69) * mm, "end": v(20.69, -6.75) * mm});
            skLineSegment(sketch, "E51.9.24", {"start": v(19.6, -8.9) * mm, "end": v(19.62, -8.9) * mm});
            skLineSegment(sketch, "E51.9.25", {"start": v(19.62, -8.9) * mm, "end": v(19.7, -8.94) * mm});
            skLineSegment(sketch, "E51.9.26", {"start": v(20.69, -6.75) * mm, "end": v(20.85, -6.84) * mm});
            skLineSegment(sketch, "E51.9.27", {"start": v(19.7, -8.94) * mm, "end": v(19.82, -8.98) * mm});
            skLineSegment(sketch, "E51.9.28", {"start": v(20.49, -6.66) * mm, "end": v(20.56, -6.69) * mm});
            skLineSegment(sketch, "E51.9.29", {"start": v(20.46, -6.65) * mm, "end": v(20.49, -6.66) * mm});
            skLineSegment(sketch, "E51.10.0", {"start": v(20.39, 0) * mm, "end": v(21.52, 0) * mm});
            skLineSegment(sketch, "E51.10.1", {"start": v(24.5, -1.6) * mm, "end": v(25.06, -1.32) * mm});
            skLineSegment(sketch, "E51.10.2", {"start": v(20.26, -2.28) * mm, "end": v(21.38, -2.4) * mm});
            skLineSegment(sketch, "E51.10.3", {"start": v(23.99, -1.82) * mm, "end": v(24.5, -1.6) * mm});
            skLineSegment(sketch, "E51.10.4", {"start": v(24.04, -0.87) * mm, "end": v(24.53, -1.16) * mm});
            skLineSegment(sketch, "E51.10.5", {"start": v(24.53, -1.16) * mm, "end": v(25.05, -1.5) * mm});
            skLineSegment(sketch, "E51.10.6", {"start": v(23.51, -2) * mm, "end": v(23.99, -1.82) * mm});
            skLineSegment(sketch, "E51.10.7", {"start": v(25.64, -0.99) * mm, "end": v(26.26, -0.6) * mm});
            skLineSegment(sketch, "E51.10.8", {"start": v(23.08, -2.15) * mm, "end": v(23.51, -2) * mm});
            skLineSegment(sketch, "E51.10.9", {"start": v(25.6, -1.89) * mm, "end": v(26.16, -2.34) * mm});
            skLineSegment(sketch, "E51.10.10", {"start": v(25.06, -1.32) * mm, "end": v(25.64, -0.99) * mm});
            skLineSegment(sketch, "E51.10.11", {"start": v(23.59, -0.64) * mm, "end": v(24.04, -0.87) * mm});
            skLineSegment(sketch, "E51.10.12", {"start": v(25.05, -1.5) * mm, "end": v(25.6, -1.89) * mm});
            skLineSegment(sketch, "E51.10.13", {"start": v(22.05, -2.37) * mm, "end": v(22.34, -2.32) * mm});
            skLineSegment(sketch, "E51.10.14", {"start": v(22.34, -2.32) * mm, "end": v(22.69, -2.25) * mm});
            skLineSegment(sketch, "E51.10.15", {"start": v(22.69, -2.25) * mm, "end": v(23.08, -2.15) * mm});
            skLineSegment(sketch, "E51.10.16", {"start": v(22.8, -0.3) * mm, "end": v(23.17, -0.45) * mm});
            skLineSegment(sketch, "E51.10.17", {"start": v(22.46, -0.2) * mm, "end": v(22.8, -0.3) * mm});
            skLineSegment(sketch, "E51.10.18", {"start": v(23.17, -0.45) * mm, "end": v(23.59, -0.64) * mm});
            skLineSegment(sketch, "E51.10.19", {"start": v(21.81, -2.4) * mm, "end": v(22.05, -2.37) * mm});
            skLineSegment(sketch, "E51.10.20", {"start": v(21.62, -2.41) * mm, "end": v(21.81, -2.4) * mm});
            skLineSegment(sketch, "E51.10.21", {"start": v(22.18, -0.11) * mm, "end": v(22.46, -0.2) * mm});
            skLineSegment(sketch, "E51.10.22", {"start": v(21.94, -0.06) * mm, "end": v(22.18, -0.11) * mm});
            skLineSegment(sketch, "E51.10.23", {"start": v(21.62, 0) * mm, "end": v(21.76, -0.02) * mm});
            skLineSegment(sketch, "E51.10.24", {"start": v(21.38, -2.4) * mm, "end": v(21.4, -2.41) * mm});
            skLineSegment(sketch, "E51.10.25", {"start": v(21.4, -2.41) * mm, "end": v(21.49, -2.41) * mm});
            skLineSegment(sketch, "E51.10.26", {"start": v(21.76, -0.02) * mm, "end": v(21.94, -0.06) * mm});
            skLineSegment(sketch, "E51.10.27", {"start": v(21.49, -2.41) * mm, "end": v(21.62, -2.41) * mm});
            skLineSegment(sketch, "E51.10.28", {"start": v(21.54, 0) * mm, "end": v(21.62, 0) * mm});
            skLineSegment(sketch, "E51.10.29", {"start": v(21.52, 0) * mm, "end": v(21.54, 0) * mm});
            skLineSegment(sketch, "E51.11.0", {"start": v(19.4, 6.3) * mm, "end": v(20.46, 6.65) * mm});
            skLineSegment(sketch, "E51.11.1", {"start": v(23.8, 6.05) * mm, "end": v(24.24, 6.49) * mm});
            skLineSegment(sketch, "E51.11.2", {"start": v(19.97, 4.09) * mm, "end": v(21.08, 4.32) * mm});
            skLineSegment(sketch, "E51.11.3", {"start": v(23.38, 5.68) * mm, "end": v(23.8, 6.05) * mm});
            skLineSegment(sketch, "E51.11.4", {"start": v(23.13, 6.6) * mm, "end": v(23.69, 6.48) * mm});
            skLineSegment(sketch, "E51.11.5", {"start": v(23.69, 6.48) * mm, "end": v(24.28, 6.32) * mm});
            skLineSegment(sketch, "E51.11.6", {"start": v(22.98, 5.36) * mm, "end": v(23.38, 5.68) * mm});
            skLineSegment(sketch, "E51.11.7", {"start": v(24.7, 6.98) * mm, "end": v(25.16, 7.54) * mm});
            skLineSegment(sketch, "E51.11.8", {"start": v(22.6, 5.1) * mm, "end": v(22.98, 5.36) * mm});
            skLineSegment(sketch, "E51.11.9", {"start": v(24.92, 6.11) * mm, "end": v(25.6, 5.86) * mm});
            skLineSegment(sketch, "E51.11.10", {"start": v(24.24, 6.49) * mm, "end": v(24.7, 6.98) * mm});
            skLineSegment(sketch, "E51.11.11", {"start": v(22.63, 6.68) * mm, "end": v(23.13, 6.6) * mm});
            skLineSegment(sketch, "E51.11.12", {"start": v(24.28, 6.32) * mm, "end": v(24.92, 6.11) * mm});
            skLineSegment(sketch, "E51.11.13", {"start": v(21.7, 4.56) * mm, "end": v(21.97, 4.7) * mm});
            skLineSegment(sketch, "E51.11.14", {"start": v(21.97, 4.7) * mm, "end": v(22.27, 4.87) * mm});
            skLineSegment(sketch, "E51.11.15", {"start": v(22.27, 4.87) * mm, "end": v(22.6, 5.1) * mm});
            skLineSegment(sketch, "E51.11.16", {"start": v(21.77, 6.76) * mm, "end": v(22.18, 6.73) * mm});
            skLineSegment(sketch, "E51.11.17", {"start": v(21.42, 6.76) * mm, "end": v(21.77, 6.76) * mm});
            skLineSegment(sketch, "E51.11.18", {"start": v(22.18, 6.73) * mm, "end": v(22.63, 6.68) * mm});
            skLineSegment(sketch, "E51.11.19", {"start": v(21.49, 4.46) * mm, "end": v(21.7, 4.56) * mm});
            skLineSegment(sketch, "E51.11.20", {"start": v(21.31, 4.39) * mm, "end": v(21.49, 4.46) * mm});
            skLineSegment(sketch, "E51.11.21", {"start": v(21.13, 6.75) * mm, "end": v(21.42, 6.76) * mm});
            skLineSegment(sketch, "E51.11.22", {"start": v(20.89, 6.73) * mm, "end": v(21.13, 6.75) * mm});
            skLineSegment(sketch, "E51.11.23", {"start": v(20.57, 6.68) * mm, "end": v(20.7, 6.7) * mm});
            skLineSegment(sketch, "E51.11.24", {"start": v(21.08, 4.32) * mm, "end": v(21.1, 4.32) * mm});
            skLineSegment(sketch, "E51.11.25", {"start": v(21.1, 4.32) * mm, "end": v(21.18, 4.34) * mm});
            skLineSegment(sketch, "E51.11.26", {"start": v(20.7, 6.7) * mm, "end": v(20.89, 6.73) * mm});
            skLineSegment(sketch, "E51.11.27", {"start": v(21.18, 4.34) * mm, "end": v(21.31, 4.39) * mm});
            skLineSegment(sketch, "E51.11.28", {"start": v(20.49, 6.66) * mm, "end": v(20.57, 6.68) * mm});
            skLineSegment(sketch, "E51.11.29", {"start": v(20.46, 6.65) * mm, "end": v(20.49, 6.66) * mm});
            skLineSegment(sketch, "E51.12.0", {"start": v(16.5, 11.98) * mm, "end": v(17.4, 12.65) * mm});
            skLineSegment(sketch, "E51.12.1", {"start": v(20.76, 13.11) * mm, "end": v(21.05, 13.66) * mm});
            skLineSegment(sketch, "E51.12.2", {"start": v(17.73, 10.06) * mm, "end": v(18.71, 10.62) * mm});
            skLineSegment(sketch, "E51.12.3", {"start": v(20.48, 12.62) * mm, "end": v(20.76, 13.11) * mm});
            skLineSegment(sketch, "E51.12.4", {"start": v(19.96, 13.42) * mm, "end": v(20.53, 13.48) * mm});
            skLineSegment(sketch, "E51.12.5", {"start": v(20.53, 13.48) * mm, "end": v(21.14, 13.51) * mm});
            skLineSegment(sketch, "E51.12.6", {"start": v(20.2, 12.2) * mm, "end": v(20.48, 12.62) * mm});
            skLineSegment(sketch, "E51.12.7", {"start": v(21.33, 14.27) * mm, "end": v(21.6, 14.95) * mm});
            skLineSegment(sketch, "E51.12.8", {"start": v(19.93, 11.83) * mm, "end": v(20.2, 12.2) * mm});
            skLineSegment(sketch, "E51.12.9", {"start": v(21.82, 13.52) * mm, "end": v(22.54, 13.48) * mm});
            skLineSegment(sketch, "E51.12.10", {"start": v(21.05, 13.66) * mm, "end": v(21.33, 14.27) * mm});
            skLineSegment(sketch, "E51.12.11", {"start": v(19.46, 13.35) * mm, "end": v(19.96, 13.42) * mm});
            skLineSegment(sketch, "E51.12.12", {"start": v(21.14, 13.51) * mm, "end": v(21.82, 13.52) * mm});
            skLineSegment(sketch, "E51.12.13", {"start": v(19.24, 11.04) * mm, "end": v(19.44, 11.25) * mm});
            skLineSegment(sketch, "E51.12.14", {"start": v(19.44, 11.25) * mm, "end": v(19.68, 11.51) * mm});
            skLineSegment(sketch, "E51.12.15", {"start": v(19.68, 11.51) * mm, "end": v(19.93, 11.83) * mm});
            skLineSegment(sketch, "E51.12.16", {"start": v(18.62, 13.15) * mm, "end": v(19.01, 13.25) * mm});
            skLineSegment(sketch, "E51.12.17", {"start": v(18.29, 13.05) * mm, "end": v(18.62, 13.15) * mm});
            skLineSegment(sketch, "E51.12.18", {"start": v(19.01, 13.25) * mm, "end": v(19.46, 13.35) * mm});
            skLineSegment(sketch, "E51.12.19", {"start": v(19.06, 10.88) * mm, "end": v(19.24, 11.04) * mm});
            skLineSegment(sketch, "E51.12.20", {"start": v(18.91, 10.76) * mm, "end": v(19.06, 10.88) * mm});
            skLineSegment(sketch, "E51.12.21", {"start": v(18, 12.95) * mm, "end": v(18.29, 13.05) * mm});
            skLineSegment(sketch, "E51.12.22", {"start": v(17.79, 12.85) * mm, "end": v(18, 12.95) * mm});
            skLineSegment(sketch, "E51.12.23", {"start": v(17.5, 12.7) * mm, "end": v(17.62, 12.77) * mm});
            skLineSegment(sketch, "E51.12.24", {"start": v(18.71, 10.62) * mm, "end": v(18.74, 10.63) * mm});
            skLineSegment(sketch, "E51.12.25", {"start": v(18.74, 10.63) * mm, "end": v(18.8, 10.68) * mm});
            skLineSegment(sketch, "E51.12.26", {"start": v(17.62, 12.77) * mm, "end": v(17.79, 12.85) * mm});
            skLineSegment(sketch, "E51.12.27", {"start": v(18.8, 10.68) * mm, "end": v(18.91, 10.76) * mm});
            skLineSegment(sketch, "E51.12.28", {"start": v(17.43, 12.66) * mm, "end": v(17.5, 12.7) * mm});
            skLineSegment(sketch, "E51.12.29", {"start": v(17.4, 12.65) * mm, "end": v(17.43, 12.66) * mm});
            skLineSegment(sketch, "E51.13.0", {"start": v(11.98, 16.5) * mm, "end": v(12.65, 17.4) * mm});
            skLineSegment(sketch, "E51.13.1", {"start": v(15.7, 18.89) * mm, "end": v(15.8, 19.5) * mm});
            skLineSegment(sketch, "E51.13.2", {"start": v(13.76, 15.05) * mm, "end": v(14.52, 15.88) * mm});
            skLineSegment(sketch, "E51.13.3", {"start": v(15.57, 18.33) * mm, "end": v(15.7, 18.89) * mm});
            skLineSegment(sketch, "E51.13.4", {"start": v(14.84, 18.94) * mm, "end": v(15.35, 19.16) * mm});
            skLineSegment(sketch, "E51.13.5", {"start": v(15.35, 19.16) * mm, "end": v(15.93, 19.39) * mm});
            skLineSegment(sketch, "E51.13.6", {"start": v(15.44, 17.84) * mm, "end": v(15.57, 18.33) * mm});
            skLineSegment(sketch, "E51.13.7", {"start": v(15.87, 20.16) * mm, "end": v(15.92, 20.89) * mm});
            skLineSegment(sketch, "E51.13.8", {"start": v(15.3, 17.4) * mm, "end": v(15.44, 17.84) * mm});
            skLineSegment(sketch, "E51.13.9", {"start": v(16.57, 19.6) * mm, "end": v(17.27, 19.79) * mm});
            skLineSegment(sketch, "E51.13.10", {"start": v(15.8, 19.5) * mm, "end": v(15.87, 20.16) * mm});
            skLineSegment(sketch, "E51.13.11", {"start": v(14.38, 18.7) * mm, "end": v(14.84, 18.94) * mm});
            skLineSegment(sketch, "E51.13.12", {"start": v(15.93, 19.39) * mm, "end": v(16.57, 19.6) * mm});
            skLineSegment(sketch, "E51.13.13", {"start": v(14.88, 16.45) * mm, "end": v(15.01, 16.71) * mm});
            skLineSegment(sketch, "E51.13.14", {"start": v(15.01, 16.71) * mm, "end": v(15.15, 17.03) * mm});
            skLineSegment(sketch, "E51.13.15", {"start": v(15.15, 17.03) * mm, "end": v(15.3, 17.4) * mm});
            skLineSegment(sketch, "E51.13.16", {"start": v(13.64, 18.26) * mm, "end": v(13.98, 18.48) * mm});
            skLineSegment(sketch, "E51.13.17", {"start": v(13.36, 18.06) * mm, "end": v(13.64, 18.26) * mm});
            skLineSegment(sketch, "E51.13.18", {"start": v(13.98, 18.48) * mm, "end": v(14.38, 18.7) * mm});
            skLineSegment(sketch, "E51.13.19", {"start": v(14.76, 16.24) * mm, "end": v(14.88, 16.45) * mm});
            skLineSegment(sketch, "E51.13.20", {"start": v(14.66, 16.08) * mm, "end": v(14.76, 16.24) * mm});
            skLineSegment(sketch, "E51.13.21", {"start": v(13.13, 17.88) * mm, "end": v(13.36, 18.06) * mm});
            skLineSegment(sketch, "E51.13.22", {"start": v(12.94, 17.72) * mm, "end": v(13.13, 17.88) * mm});
            skLineSegment(sketch, "E51.13.23", {"start": v(12.72, 17.5) * mm, "end": v(12.8, 17.59) * mm});
            skLineSegment(sketch, "E51.13.24", {"start": v(14.52, 15.88) * mm, "end": v(14.53, 15.9) * mm});
            skLineSegment(sketch, "E51.13.25", {"start": v(14.53, 15.9) * mm, "end": v(14.58, 15.97) * mm});
            skLineSegment(sketch, "E51.13.26", {"start": v(12.8, 17.59) * mm, "end": v(12.94, 17.72) * mm});
            skLineSegment(sketch, "E51.13.27", {"start": v(14.58, 15.97) * mm, "end": v(14.66, 16.08) * mm});
            skLineSegment(sketch, "E51.13.28", {"start": v(12.66, 17.43) * mm, "end": v(12.72, 17.5) * mm});
            skLineSegment(sketch, "E51.13.29", {"start": v(12.65, 17.4) * mm, "end": v(12.66, 17.43) * mm});
            skLineSegment(sketch, "E51.14.0", {"start": v(6.3, 19.4) * mm, "end": v(6.65, 20.46) * mm});
            skLineSegment(sketch, "E51.14.1", {"start": v(9.1, 22.81) * mm, "end": v(9, 23.42) * mm});
            skLineSegment(sketch, "E51.14.2", {"start": v(8.43, 18.56) * mm, "end": v(8.9, 19.6) * mm});
            skLineSegment(sketch, "E51.14.3", {"start": v(9.15, 22.25) * mm, "end": v(9.1, 22.81) * mm});
            skLineSegment(sketch, "E51.14.4", {"start": v(8.26, 22.6) * mm, "end": v(8.68, 22.97) * mm});
            skLineSegment(sketch, "E51.14.5", {"start": v(8.68, 22.97) * mm, "end": v(9.16, 23.36) * mm});
            skLineSegment(sketch, "E51.14.6", {"start": v(9.17, 21.74) * mm, "end": v(9.15, 22.25) * mm});
            skLineSegment(sketch, "E51.14.7", {"start": v(8.87, 24.08) * mm, "end": v(8.69, 24.79) * mm});
            skLineSegment(sketch, "E51.14.8", {"start": v(9.17, 21.28) * mm, "end": v(9.17, 21.74) * mm});
            skLineSegment(sketch, "E51.14.9", {"start": v(9.7, 23.76) * mm, "end": v(10.31, 24.16) * mm});
            skLineSegment(sketch, "E51.14.10", {"start": v(9, 23.42) * mm, "end": v(8.87, 24.08) * mm});
            skLineSegment(sketch, "E51.14.11", {"start": v(7.9, 22.23) * mm, "end": v(8.26, 22.6) * mm});
            skLineSegment(sketch, "E51.14.12", {"start": v(9.16, 23.36) * mm, "end": v(9.7, 23.76) * mm});
            skLineSegment(sketch, "E51.14.13", {"start": v(9.07, 20.24) * mm, "end": v(9.12, 20.53) * mm});
            skLineSegment(sketch, "E51.14.14", {"start": v(9.12, 20.53) * mm, "end": v(9.15, 20.88) * mm});
            skLineSegment(sketch, "E51.14.15", {"start": v(9.15, 20.88) * mm, "end": v(9.17, 21.28) * mm});
            skLineSegment(sketch, "E51.14.16", {"start": v(7.33, 21.59) * mm, "end": v(7.59, 21.9) * mm});
            skLineSegment(sketch, "E51.14.17", {"start": v(7.12, 21.3) * mm, "end": v(7.33, 21.59) * mm});
            skLineSegment(sketch, "E51.14.18", {"start": v(7.59, 21.9) * mm, "end": v(7.9, 22.23) * mm});
            skLineSegment(sketch, "E51.14.19", {"start": v(9.02, 20) * mm, "end": v(9.07, 20.24) * mm});
            skLineSegment(sketch, "E51.14.20", {"start": v(8.98, 19.82) * mm, "end": v(9.02, 20) * mm});
            skLineSegment(sketch, "E51.14.21", {"start": v(6.96, 21.06) * mm, "end": v(7.12, 21.3) * mm});
            skLineSegment(sketch, "E51.14.22", {"start": v(6.84, 20.85) * mm, "end": v(6.96, 21.06) * mm});
            skLineSegment(sketch, "E51.14.23", {"start": v(6.69, 20.56) * mm, "end": v(6.75, 20.69) * mm});
            skLineSegment(sketch, "E51.14.24", {"start": v(8.9, 19.6) * mm, "end": v(8.9, 19.62) * mm});
            skLineSegment(sketch, "E51.14.25", {"start": v(8.9, 19.62) * mm, "end": v(8.94, 19.7) * mm});
            skLineSegment(sketch, "E51.14.26", {"start": v(6.75, 20.69) * mm, "end": v(6.84, 20.85) * mm});
            skLineSegment(sketch, "E51.14.27", {"start": v(8.94, 19.7) * mm, "end": v(8.98, 19.82) * mm});
            skLineSegment(sketch, "E51.14.28", {"start": v(6.66, 20.49) * mm, "end": v(6.69, 20.56) * mm});
            skLineSegment(sketch, "E51.14.29", {"start": v(6.65, 20.46) * mm, "end": v(6.66, 20.49) * mm});
            skLineSegment(sketch, "E51.15.0", {"start": v(0, 20.39) * mm, "end": v(0, 21.52) * mm});
            skLineSegment(sketch, "E51.15.1", {"start": v(1.6, 24.5) * mm, "end": v(1.32, 25.06) * mm});
            skLineSegment(sketch, "E51.15.2", {"start": v(2.28, 20.26) * mm, "end": v(2.4, 21.38) * mm});
            skLineSegment(sketch, "E51.15.3", {"start": v(1.82, 23.99) * mm, "end": v(1.6, 24.5) * mm});
            skLineSegment(sketch, "E51.15.4", {"start": v(0.87, 24.04) * mm, "end": v(1.16, 24.53) * mm});
            skLineSegment(sketch, "E51.15.5", {"start": v(1.16, 24.53) * mm, "end": v(1.5, 25.05) * mm});
            skLineSegment(sketch, "E51.15.6", {"start": v(2, 23.51) * mm, "end": v(1.82, 23.99) * mm});
            skLineSegment(sketch, "E51.15.7", {"start": v(0.99, 25.64) * mm, "end": v(0.6, 26.26) * mm});
            skLineSegment(sketch, "E51.15.8", {"start": v(2.15, 23.08) * mm, "end": v(2, 23.51) * mm});
            skLineSegment(sketch, "E51.15.9", {"start": v(1.89, 25.6) * mm, "end": v(2.34, 26.16) * mm});
            skLineSegment(sketch, "E51.15.10", {"start": v(1.32, 25.06) * mm, "end": v(0.99, 25.64) * mm});
            skLineSegment(sketch, "E51.15.11", {"start": v(0.64, 23.59) * mm, "end": v(0.87, 24.04) * mm});
            skLineSegment(sketch, "E51.15.12", {"start": v(1.5, 25.05) * mm, "end": v(1.89, 25.6) * mm});
            skLineSegment(sketch, "E51.15.13", {"start": v(2.37, 22.05) * mm, "end": v(2.32, 22.34) * mm});
            skLineSegment(sketch, "E51.15.14", {"start": v(2.32, 22.34) * mm, "end": v(2.25, 22.69) * mm});
            skLineSegment(sketch, "E51.15.15", {"start": v(2.25, 22.69) * mm, "end": v(2.15, 23.08) * mm});
            skLineSegment(sketch, "E51.15.16", {"start": v(0.3, 22.8) * mm, "end": v(0.45, 23.17) * mm});
            skLineSegment(sketch, "E51.15.17", {"start": v(0.2, 22.46) * mm, "end": v(0.3, 22.8) * mm});
            skLineSegment(sketch, "E51.15.18", {"start": v(0.45, 23.17) * mm, "end": v(0.64, 23.59) * mm});
            skLineSegment(sketch, "E51.15.19", {"start": v(2.4, 21.81) * mm, "end": v(2.37, 22.05) * mm});
            skLineSegment(sketch, "E51.15.20", {"start": v(2.41, 21.62) * mm, "end": v(2.4, 21.81) * mm});
            skLineSegment(sketch, "E51.15.21", {"start": v(0.11, 22.18) * mm, "end": v(0.2, 22.46) * mm});
            skLineSegment(sketch, "E51.15.22", {"start": v(0.06, 21.94) * mm, "end": v(0.11, 22.18) * mm});
            skLineSegment(sketch, "E51.15.23", {"start": v(0, 21.62) * mm, "end": v(0.02, 21.76) * mm});
            skLineSegment(sketch, "E51.15.24", {"start": v(2.4, 21.38) * mm, "end": v(2.41, 21.4) * mm});
            skLineSegment(sketch, "E51.15.25", {"start": v(2.41, 21.4) * mm, "end": v(2.41, 21.49) * mm});
            skLineSegment(sketch, "E51.15.26", {"start": v(0.02, 21.76) * mm, "end": v(0.06, 21.94) * mm});
            skLineSegment(sketch, "E51.15.27", {"start": v(2.41, 21.49) * mm, "end": v(2.41, 21.62) * mm});
            skLineSegment(sketch, "E51.15.28", {"start": v(0, 21.54) * mm, "end": v(0, 21.62) * mm});
            skLineSegment(sketch, "E51.15.29", {"start": v(0, 21.52) * mm, "end": v(0, 21.54) * mm});
            skLineSegment(sketch, "E51.16.0", {"start": v(-6.3, 19.4) * mm, "end": v(-6.65, 20.46) * mm});
            skLineSegment(sketch, "E51.16.1", {"start": v(-6.05, 23.8) * mm, "end": v(-6.49, 24.24) * mm});
            skLineSegment(sketch, "E51.16.2", {"start": v(-4.09, 19.97) * mm, "end": v(-4.32, 21.08) * mm});
            skLineSegment(sketch, "E51.16.3", {"start": v(-5.68, 23.38) * mm, "end": v(-6.05, 23.8) * mm});
            skLineSegment(sketch, "E51.16.4", {"start": v(-6.6, 23.13) * mm, "end": v(-6.48, 23.69) * mm});
            skLineSegment(sketch, "E51.16.5", {"start": v(-6.48, 23.69) * mm, "end": v(-6.32, 24.28) * mm});
            skLineSegment(sketch, "E51.16.6", {"start": v(-5.36, 22.98) * mm, "end": v(-5.68, 23.38) * mm});
            skLineSegment(sketch, "E51.16.7", {"start": v(-6.98, 24.7) * mm, "end": v(-7.54, 25.16) * mm});
            skLineSegment(sketch, "E51.16.8", {"start": v(-5.1, 22.6) * mm, "end": v(-5.36, 22.98) * mm});
            skLineSegment(sketch, "E51.16.9", {"start": v(-6.11, 24.92) * mm, "end": v(-5.86, 25.6) * mm});
            skLineSegment(sketch, "E51.16.10", {"start": v(-6.49, 24.24) * mm, "end": v(-6.98, 24.7) * mm});
            skLineSegment(sketch, "E51.16.11", {"start": v(-6.68, 22.63) * mm, "end": v(-6.6, 23.13) * mm});
            skLineSegment(sketch, "E51.16.12", {"start": v(-6.32, 24.28) * mm, "end": v(-6.11, 24.92) * mm});
            skLineSegment(sketch, "E51.16.13", {"start": v(-4.56, 21.7) * mm, "end": v(-4.7, 21.97) * mm});
            skLineSegment(sketch, "E51.16.14", {"start": v(-4.7, 21.97) * mm, "end": v(-4.87, 22.27) * mm});
            skLineSegment(sketch, "E51.16.15", {"start": v(-4.87, 22.27) * mm, "end": v(-5.1, 22.6) * mm});
            skLineSegment(sketch, "E51.16.16", {"start": v(-6.76, 21.77) * mm, "end": v(-6.73, 22.18) * mm});
            skLineSegment(sketch, "E51.16.17", {"start": v(-6.76, 21.42) * mm, "end": v(-6.76, 21.77) * mm});
            skLineSegment(sketch, "E51.16.18", {"start": v(-6.73, 22.18) * mm, "end": v(-6.68, 22.63) * mm});
            skLineSegment(sketch, "E51.16.19", {"start": v(-4.46, 21.49) * mm, "end": v(-4.56, 21.7) * mm});
            skLineSegment(sketch, "E51.16.20", {"start": v(-4.39, 21.31) * mm, "end": v(-4.46, 21.49) * mm});
            skLineSegment(sketch, "E51.16.21", {"start": v(-6.75, 21.13) * mm, "end": v(-6.76, 21.42) * mm});
            skLineSegment(sketch, "E51.16.22", {"start": v(-6.73, 20.89) * mm, "end": v(-6.75, 21.13) * mm});
            skLineSegment(sketch, "E51.16.23", {"start": v(-6.68, 20.57) * mm, "end": v(-6.7, 20.7) * mm});
            skLineSegment(sketch, "E51.16.24", {"start": v(-4.32, 21.08) * mm, "end": v(-4.32, 21.1) * mm});
            skLineSegment(sketch, "E51.16.25", {"start": v(-4.32, 21.1) * mm, "end": v(-4.34, 21.18) * mm});
            skLineSegment(sketch, "E51.16.26", {"start": v(-6.7, 20.7) * mm, "end": v(-6.73, 20.89) * mm});
            skLineSegment(sketch, "E51.16.27", {"start": v(-4.34, 21.18) * mm, "end": v(-4.39, 21.31) * mm});
            skLineSegment(sketch, "E51.16.28", {"start": v(-6.66, 20.49) * mm, "end": v(-6.68, 20.57) * mm});
            skLineSegment(sketch, "E51.16.29", {"start": v(-6.65, 20.46) * mm, "end": v(-6.66, 20.49) * mm});
            skLineSegment(sketch, "E51.17.0", {"start": v(-11.98, 16.5) * mm, "end": v(-12.65, 17.4) * mm});
            skLineSegment(sketch, "E51.17.1", {"start": v(-13.11, 20.76) * mm, "end": v(-13.66, 21.05) * mm});
            skLineSegment(sketch, "E51.17.2", {"start": v(-10.06, 17.73) * mm, "end": v(-10.62, 18.71) * mm});
            skLineSegment(sketch, "E51.17.3", {"start": v(-12.62, 20.48) * mm, "end": v(-13.11, 20.76) * mm});
            skLineSegment(sketch, "E51.17.4", {"start": v(-13.42, 19.96) * mm, "end": v(-13.48, 20.53) * mm});
            skLineSegment(sketch, "E51.17.5", {"start": v(-13.48, 20.53) * mm, "end": v(-13.51, 21.14) * mm});
            skLineSegment(sketch, "E51.17.6", {"start": v(-12.2, 20.2) * mm, "end": v(-12.62, 20.48) * mm});
            skLineSegment(sketch, "E51.17.7", {"start": v(-14.27, 21.33) * mm, "end": v(-14.95, 21.6) * mm});
            skLineSegment(sketch, "E51.17.8", {"start": v(-11.83, 19.93) * mm, "end": v(-12.2, 20.2) * mm});
            skLineSegment(sketch, "E51.17.9", {"start": v(-13.52, 21.82) * mm, "end": v(-13.48, 22.54) * mm});
            skLineSegment(sketch, "E51.17.10", {"start": v(-13.66, 21.05) * mm, "end": v(-14.27, 21.33) * mm});
            skLineSegment(sketch, "E51.17.11", {"start": v(-13.35, 19.46) * mm, "end": v(-13.42, 19.96) * mm});
            skLineSegment(sketch, "E51.17.12", {"start": v(-13.51, 21.14) * mm, "end": v(-13.52, 21.82) * mm});
            skLineSegment(sketch, "E51.17.13", {"start": v(-11.04, 19.24) * mm, "end": v(-11.25, 19.44) * mm});
            skLineSegment(sketch, "E51.17.14", {"start": v(-11.25, 19.44) * mm, "end": v(-11.51, 19.68) * mm});
            skLineSegment(sketch, "E51.17.15", {"start": v(-11.51, 19.68) * mm, "end": v(-11.83, 19.93) * mm});
            skLineSegment(sketch, "E51.17.16", {"start": v(-13.15, 18.62) * mm, "end": v(-13.25, 19.01) * mm});
            skLineSegment(sketch, "E51.17.17", {"start": v(-13.05, 18.29) * mm, "end": v(-13.15, 18.62) * mm});
            skLineSegment(sketch, "E51.17.18", {"start": v(-13.25, 19.01) * mm, "end": v(-13.35, 19.46) * mm});
            skLineSegment(sketch, "E51.17.19", {"start": v(-10.88, 19.06) * mm, "end": v(-11.04, 19.24) * mm});
            skLineSegment(sketch, "E51.17.20", {"start": v(-10.76, 18.91) * mm, "end": v(-10.88, 19.06) * mm});
            skLineSegment(sketch, "E51.17.21", {"start": v(-12.95, 18) * mm, "end": v(-13.05, 18.29) * mm});
            skLineSegment(sketch, "E51.17.22", {"start": v(-12.85, 17.79) * mm, "end": v(-12.95, 18) * mm});
            skLineSegment(sketch, "E51.17.23", {"start": v(-12.7, 17.5) * mm, "end": v(-12.77, 17.62) * mm});
            skLineSegment(sketch, "E51.17.24", {"start": v(-10.62, 18.71) * mm, "end": v(-10.63, 18.74) * mm});
            skLineSegment(sketch, "E51.17.25", {"start": v(-10.63, 18.74) * mm, "end": v(-10.68, 18.8) * mm});
            skLineSegment(sketch, "E51.17.26", {"start": v(-12.77, 17.62) * mm, "end": v(-12.85, 17.79) * mm});
            skLineSegment(sketch, "E51.17.27", {"start": v(-10.68, 18.8) * mm, "end": v(-10.76, 18.91) * mm});
            skLineSegment(sketch, "E51.17.28", {"start": v(-12.66, 17.43) * mm, "end": v(-12.7, 17.5) * mm});
            skLineSegment(sketch, "E51.17.29", {"start": v(-12.65, 17.4) * mm, "end": v(-12.66, 17.43) * mm});
            skLineSegment(sketch, "E51.18.0", {"start": v(-16.5, 11.98) * mm, "end": v(-17.4, 12.65) * mm});
            skLineSegment(sketch, "E51.18.1", {"start": v(-18.89, 15.7) * mm, "end": v(-19.5, 15.8) * mm});
            skLineSegment(sketch, "E51.18.2", {"start": v(-15.05, 13.76) * mm, "end": v(-15.88, 14.52) * mm});
            skLineSegment(sketch, "E51.18.3", {"start": v(-18.33, 15.57) * mm, "end": v(-18.89, 15.7) * mm});
            skLineSegment(sketch, "E51.18.4", {"start": v(-18.94, 14.84) * mm, "end": v(-19.16, 15.35) * mm});
            skLineSegment(sketch, "E51.18.5", {"start": v(-19.16, 15.35) * mm, "end": v(-19.39, 15.93) * mm});
            skLineSegment(sketch, "E51.18.6", {"start": v(-17.84, 15.44) * mm, "end": v(-18.33, 15.57) * mm});
            skLineSegment(sketch, "E51.18.7", {"start": v(-20.16, 15.87) * mm, "end": v(-20.89, 15.92) * mm});
            skLineSegment(sketch, "E51.18.8", {"start": v(-17.4, 15.3) * mm, "end": v(-17.84, 15.44) * mm});
            skLineSegment(sketch, "E51.18.9", {"start": v(-19.6, 16.57) * mm, "end": v(-19.79, 17.27) * mm});
            skLineSegment(sketch, "E51.18.10", {"start": v(-19.5, 15.8) * mm, "end": v(-20.16, 15.87) * mm});
            skLineSegment(sketch, "E51.18.11", {"start": v(-18.7, 14.38) * mm, "end": v(-18.94, 14.84) * mm});
            skLineSegment(sketch, "E51.18.12", {"start": v(-19.39, 15.93) * mm, "end": v(-19.6, 16.57) * mm});
            skLineSegment(sketch, "E51.18.13", {"start": v(-16.45, 14.88) * mm, "end": v(-16.71, 15.01) * mm});
            skLineSegment(sketch, "E51.18.14", {"start": v(-16.71, 15.01) * mm, "end": v(-17.03, 15.15) * mm});
            skLineSegment(sketch, "E51.18.15", {"start": v(-17.03, 15.15) * mm, "end": v(-17.4, 15.3) * mm});
            skLineSegment(sketch, "E51.18.16", {"start": v(-18.26, 13.64) * mm, "end": v(-18.48, 13.98) * mm});
            skLineSegment(sketch, "E51.18.17", {"start": v(-18.06, 13.36) * mm, "end": v(-18.26, 13.64) * mm});
            skLineSegment(sketch, "E51.18.18", {"start": v(-18.48, 13.98) * mm, "end": v(-18.7, 14.38) * mm});
            skLineSegment(sketch, "E51.18.19", {"start": v(-16.24, 14.76) * mm, "end": v(-16.45, 14.88) * mm});
            skLineSegment(sketch, "E51.18.20", {"start": v(-16.08, 14.66) * mm, "end": v(-16.24, 14.76) * mm});
            skLineSegment(sketch, "E51.18.21", {"start": v(-17.88, 13.13) * mm, "end": v(-18.06, 13.36) * mm});
            skLineSegment(sketch, "E51.18.22", {"start": v(-17.72, 12.94) * mm, "end": v(-17.88, 13.13) * mm});
            skLineSegment(sketch, "E51.18.23", {"start": v(-17.5, 12.72) * mm, "end": v(-17.59, 12.8) * mm});
            skLineSegment(sketch, "E51.18.24", {"start": v(-15.88, 14.52) * mm, "end": v(-15.9, 14.53) * mm});
            skLineSegment(sketch, "E51.18.25", {"start": v(-15.9, 14.53) * mm, "end": v(-15.97, 14.58) * mm});
            skLineSegment(sketch, "E51.18.26", {"start": v(-17.59, 12.8) * mm, "end": v(-17.72, 12.94) * mm});
            skLineSegment(sketch, "E51.18.27", {"start": v(-15.97, 14.58) * mm, "end": v(-16.08, 14.66) * mm});
            skLineSegment(sketch, "E51.18.28", {"start": v(-17.43, 12.66) * mm, "end": v(-17.5, 12.72) * mm});
            skLineSegment(sketch, "E51.18.29", {"start": v(-17.4, 12.65) * mm, "end": v(-17.43, 12.66) * mm});
            skLineSegment(sketch, "E51.19.0", {"start": v(-19.4, 6.3) * mm, "end": v(-20.46, 6.65) * mm});
            skLineSegment(sketch, "E51.19.1", {"start": v(-22.81, 9.1) * mm, "end": v(-23.42, 9) * mm});
            skLineSegment(sketch, "E51.19.2", {"start": v(-18.56, 8.43) * mm, "end": v(-19.6, 8.9) * mm});
            skLineSegment(sketch, "E51.19.3", {"start": v(-22.25, 9.15) * mm, "end": v(-22.81, 9.1) * mm});
            skLineSegment(sketch, "E51.19.4", {"start": v(-22.6, 8.26) * mm, "end": v(-22.97, 8.68) * mm});
            skLineSegment(sketch, "E51.19.5", {"start": v(-22.97, 8.68) * mm, "end": v(-23.36, 9.16) * mm});
            skLineSegment(sketch, "E51.19.6", {"start": v(-21.74, 9.17) * mm, "end": v(-22.25, 9.15) * mm});
            skLineSegment(sketch, "E51.19.7", {"start": v(-24.08, 8.87) * mm, "end": v(-24.79, 8.69) * mm});
            skLineSegment(sketch, "E51.19.8", {"start": v(-21.28, 9.17) * mm, "end": v(-21.74, 9.17) * mm});
            skLineSegment(sketch, "E51.19.9", {"start": v(-23.76, 9.7) * mm, "end": v(-24.16, 10.31) * mm});
            skLineSegment(sketch, "E51.19.10", {"start": v(-23.42, 9) * mm, "end": v(-24.08, 8.87) * mm});
            skLineSegment(sketch, "E51.19.11", {"start": v(-22.23, 7.9) * mm, "end": v(-22.6, 8.26) * mm});
            skLineSegment(sketch, "E51.19.12", {"start": v(-23.36, 9.16) * mm, "end": v(-23.76, 9.7) * mm});
            skLineSegment(sketch, "E51.19.13", {"start": v(-20.24, 9.07) * mm, "end": v(-20.53, 9.12) * mm});
            skLineSegment(sketch, "E51.19.14", {"start": v(-20.53, 9.12) * mm, "end": v(-20.88, 9.15) * mm});
            skLineSegment(sketch, "E51.19.15", {"start": v(-20.88, 9.15) * mm, "end": v(-21.28, 9.17) * mm});
            skLineSegment(sketch, "E51.19.16", {"start": v(-21.59, 7.33) * mm, "end": v(-21.9, 7.59) * mm});
            skLineSegment(sketch, "E51.19.17", {"start": v(-21.3, 7.12) * mm, "end": v(-21.59, 7.33) * mm});
            skLineSegment(sketch, "E51.19.18", {"start": v(-21.9, 7.59) * mm, "end": v(-22.23, 7.9) * mm});
            skLineSegment(sketch, "E51.19.19", {"start": v(-20, 9.02) * mm, "end": v(-20.24, 9.07) * mm});
            skLineSegment(sketch, "E51.19.20", {"start": v(-19.82, 8.98) * mm, "end": v(-20, 9.02) * mm});
            skLineSegment(sketch, "E51.19.21", {"start": v(-21.06, 6.96) * mm, "end": v(-21.3, 7.12) * mm});
            skLineSegment(sketch, "E51.19.22", {"start": v(-20.85, 6.84) * mm, "end": v(-21.06, 6.96) * mm});
            skLineSegment(sketch, "E51.19.23", {"start": v(-20.56, 6.69) * mm, "end": v(-20.69, 6.75) * mm});
            skLineSegment(sketch, "E51.19.24", {"start": v(-19.6, 8.9) * mm, "end": v(-19.62, 8.9) * mm});
            skLineSegment(sketch, "E51.19.25", {"start": v(-19.62, 8.9) * mm, "end": v(-19.7, 8.94) * mm});
            skLineSegment(sketch, "E51.19.26", {"start": v(-20.69, 6.75) * mm, "end": v(-20.85, 6.84) * mm});
            skLineSegment(sketch, "E51.19.27", {"start": v(-19.7, 8.94) * mm, "end": v(-19.82, 8.98) * mm});
            skLineSegment(sketch, "E51.19.28", {"start": v(-20.49, 6.66) * mm, "end": v(-20.56, 6.69) * mm});
            skLineSegment(sketch, "E51.19.29", {"start": v(-20.46, 6.65) * mm, "end": v(-20.49, 6.66) * mm});
            skSolve(sketch);
        }
        {
            var Q0;
            {var subQ0=sQuery(id+"F1.wireOp",EDGE,"E0");var subQ27=makeQuery(id+"F1.imprint","INTERSECT",VERTEX,{"derivedFrom":[subQ0,sQuery(id+"F1.wireOp",EDGE,"E51.10.0")]});Q0=makeQuery(id+"F1.imprint","IMPRINT",FACE,{"disambiguationData":[TD([[makeQuery(id+"F1.imprint","IMPRINT",EDGE,{"disambiguationData":[TD([[subQ27,-1.0]])],"derivedFrom":subQ0}),1.0]])]});}
            var Q1;
            {var subQ0=sQuery(id+"F1.wireOp",EDGE,"E51.1.0");Q1=makeQuery(id+"F1.imprint","IMPRINT",FACE,{"disambiguationData":[TD([[makeQuery(id+"F1.imprint","IMPRINT",EDGE,{"derivedFrom":subQ0}),-1.0]])]});}
            var Q2;
            {var subQ7=sQuery(id+"F1.wireOp",EDGE,"E51.2.0");Q2=makeQuery(id+"F1.imprint","IMPRINT",FACE,{"disambiguationData":[TD([[makeQuery(id+"F1.imprint","IMPRINT",EDGE,{"derivedFrom":subQ7}),-1.0]])]});}
            var Q3;
            {var subQ8=sQuery(id+"F1.wireOp",EDGE,"E51.3.0");Q3=makeQuery(id+"F1.imprint","IMPRINT",FACE,{"disambiguationData":[TD([[makeQuery(id+"F1.imprint","IMPRINT",EDGE,{"derivedFrom":subQ8}),-1.0]])]});}
            var Q4;
            {var subQ2=sQuery(id+"F1.wireOp",EDGE,"E51.4.0");Q4=makeQuery(id+"F1.imprint","IMPRINT",FACE,{"disambiguationData":[TD([[makeQuery(id+"F1.imprint","IMPRINT",EDGE,{"derivedFrom":subQ2}),-1.0]])]});}
            var Q5;
            {var subQ8=sQuery(id+"F1.wireOp",EDGE,"E51.5.0");Q5=makeQuery(id+"F1.imprint","IMPRINT",FACE,{"disambiguationData":[TD([[makeQuery(id+"F1.imprint","IMPRINT",EDGE,{"derivedFrom":subQ8}),-1.0]])]});}
            var Q6;
            {var subQ3=sQuery(id+"F1.wireOp",EDGE,"E51.6.0");Q6=makeQuery(id+"F1.imprint","IMPRINT",FACE,{"disambiguationData":[TD([[makeQuery(id+"F1.imprint","IMPRINT",EDGE,{"derivedFrom":subQ3}),-1.0]])]});}
            var Q7;
            {var subQ0=sQuery(id+"F1.wireOp",EDGE,"E51.7.0");Q7=makeQuery(id+"F1.imprint","IMPRINT",FACE,{"disambiguationData":[TD([[makeQuery(id+"F1.imprint","IMPRINT",EDGE,{"derivedFrom":subQ0}),-1.0]])]});}
            var Q8;
            {var subQ5=sQuery(id+"F1.wireOp",EDGE,"E51.8.0");Q8=makeQuery(id+"F1.imprint","IMPRINT",FACE,{"disambiguationData":[TD([[makeQuery(id+"F1.imprint","IMPRINT",EDGE,{"derivedFrom":subQ5}),-1.0]])]});}
            var Q9;
            {var subQ1=sQuery(id+"F1.wireOp",EDGE,"E51.9.0");Q9=makeQuery(id+"F1.imprint","IMPRINT",FACE,{"disambiguationData":[TD([[makeQuery(id+"F1.imprint","IMPRINT",EDGE,{"derivedFrom":subQ1}),-1.0]])]});}
            var Q10;
            {var subQ5=sQuery(id+"F1.wireOp",EDGE,"E51.10.0");Q10=makeQuery(id+"F1.imprint","IMPRINT",FACE,{"disambiguationData":[TD([[makeQuery(id+"F1.imprint","IMPRINT",EDGE,{"derivedFrom":subQ5}),-1.0]])]});}
            var Q11;
            {var subQ8=sQuery(id+"F1.wireOp",EDGE,"E51.11.0");Q11=makeQuery(id+"F1.imprint","IMPRINT",FACE,{"disambiguationData":[TD([[makeQuery(id+"F1.imprint","IMPRINT",EDGE,{"derivedFrom":subQ8}),-1.0]])]});}
            var Q12;
            {var subQ2=sQuery(id+"F1.wireOp",EDGE,"E51.12.0");Q12=makeQuery(id+"F1.imprint","IMPRINT",FACE,{"disambiguationData":[TD([[makeQuery(id+"F1.imprint","IMPRINT",EDGE,{"derivedFrom":subQ2}),-1.0]])]});}
            var Q13;
            {var subQ3=sQuery(id+"F1.wireOp",EDGE,"E51.13.0");Q13=makeQuery(id+"F1.imprint","IMPRINT",FACE,{"disambiguationData":[TD([[makeQuery(id+"F1.imprint","IMPRINT",EDGE,{"derivedFrom":subQ3}),-1.0]])]});}
            var Q14;
            {var subQ0=sQuery(id+"F1.wireOp",EDGE,"E51.14.0");Q14=makeQuery(id+"F1.imprint","IMPRINT",FACE,{"disambiguationData":[TD([[makeQuery(id+"F1.imprint","IMPRINT",EDGE,{"derivedFrom":subQ0}),-1.0]])]});}
            var Q15;
            {var subQ6=sQuery(id+"F1.wireOp",EDGE,"E51.15.0");Q15=makeQuery(id+"F1.imprint","IMPRINT",FACE,{"disambiguationData":[TD([[makeQuery(id+"F1.imprint","IMPRINT",EDGE,{"derivedFrom":subQ6}),-1.0]])]});}
            var Q16;
            {var subQ5=sQuery(id+"F1.wireOp",EDGE,"E51.16.0");Q16=makeQuery(id+"F1.imprint","IMPRINT",FACE,{"disambiguationData":[TD([[makeQuery(id+"F1.imprint","IMPRINT",EDGE,{"derivedFrom":subQ5}),-1.0]])]});}
            var Q17;
            {var subQ7=sQuery(id+"F1.wireOp",EDGE,"E51.17.0");Q17=makeQuery(id+"F1.imprint","IMPRINT",FACE,{"disambiguationData":[TD([[makeQuery(id+"F1.imprint","IMPRINT",EDGE,{"derivedFrom":subQ7}),-1.0]])]});}
            var Q18;
            {var subQ5=sQuery(id+"F1.wireOp",EDGE,"E51.18.0");Q18=makeQuery(id+"F1.imprint","IMPRINT",FACE,{"disambiguationData":[TD([[makeQuery(id+"F1.imprint","IMPRINT",EDGE,{"derivedFrom":subQ5}),-1.0]])]});}
            var Q19;
            {var subQ8=sQuery(id+"F1.wireOp",EDGE,"E51.19.0");Q19=makeQuery(id+"F1.imprint","IMPRINT",FACE,{"disambiguationData":[TD([[makeQuery(id+"F1.imprint","IMPRINT",EDGE,{"derivedFrom":subQ8}),-1.0]])]});}
            var Q20;
            {var subQ8=sQuery(id+"F1.wireOp",EDGE,"E21");Q20=makeQuery(id+"F1.imprint","IMPRINT",FACE,{"disambiguationData":[TD([[makeQuery(id+"F1.imprint","IMPRINT",EDGE,{"derivedFrom":subQ8}),-1.0]])]});}
            extrude(context, id + "F2", {"entities" : qUnion([Q0, Q1, Q2, Q3, Q4, Q5, Q6, Q7, Q8, Q9, Q10, Q11, Q12, Q13, Q14, Q15, Q16, Q17, Q18, Q19, Q20]), "depth" : (getVariable(context, 'GearThickness')) * mm});
        }
    });
